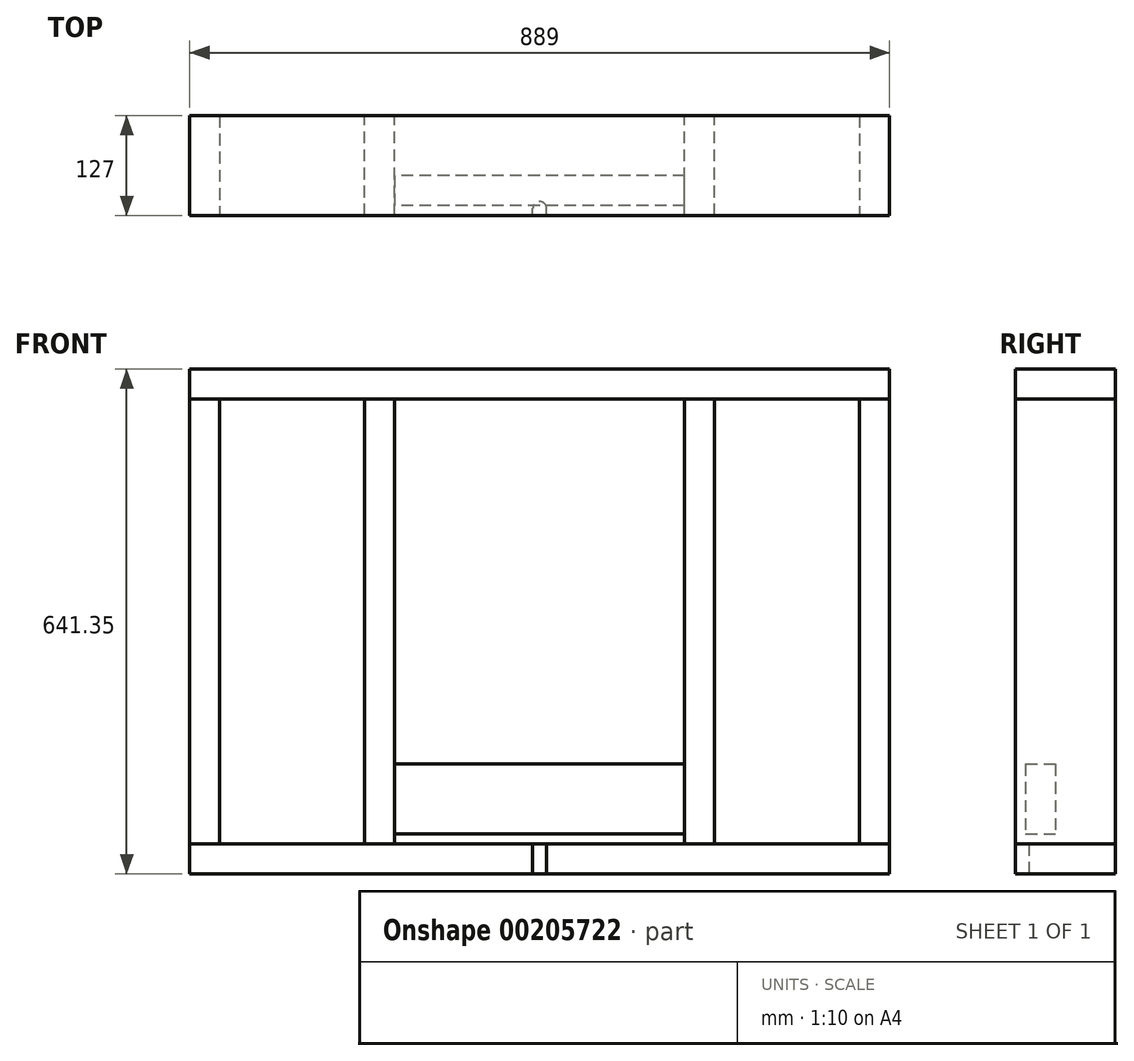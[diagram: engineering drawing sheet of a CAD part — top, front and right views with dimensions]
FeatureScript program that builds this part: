
annotation { "Feature Type Name" : "Feature", "Feature Type Description" : "" }
export const myFeature = defineFeature(function(context is Context, id is Id, definition is map)
    precondition{}
    {
        {
            var Q0;
            Q0=qCreatedBy(makeId("Top.planeOp"),FACE);
            var sketch = newSketch(context, id + "F0", { "sketchPlane" : qUnion([Q0])});
            skLineSegment(sketch, "E0.bottom", {"start": v(444.5, -63.5) * mm, "end": v(-444.5, -63.5) * mm});
            skLineSegment(sketch, "E0.top", {"start": v(444.5, 63.5) * mm, "end": v(-444.5, 63.5) * mm});
            skLineSegment(sketch, "E0.left", {"start": v(444.5, -63.5) * mm, "end": v(444.5, 63.5) * mm});
            skLineSegment(sketch, "E0.right", {"start": v(-444.5, -63.5) * mm, "end": v(-444.5, 63.5) * mm});
            skPoint(sketch, "E0.middle", {"position": v(0, 0) * mm});
            skSolve(sketch);
        }
        {
            var Q0;
            Q0 = qSketchRegion(id + "F0", true);
            extrude(context, id + "F1", {"entities" : qUnion([Q0]), "depth" : 38.1 * mm});
        }
        {
            var Q0;
            Q0=makeQuery(id+"F1.opExtrude","CAP_FACE",FACE,{"disambiguationData":[OSD([sQuery(id+"F0.wireOp",EDGE,"E0.bottom"),sQuery(id+"F0.wireOp",EDGE,"E0.top"),sQuery(id+"F0.wireOp",EDGE,"E0.left"),sQuery(id+"F0.wireOp",EDGE,"E0.right")])],"isStart":false});
            var sketch = newSketch(context, id + "F2", { "sketchPlane" : qUnion([Q0])});
            skLineSegment(sketch, "E1.bottom", {"start": v(-444.5, 63.5) * mm, "end": v(-406.4, 63.5) * mm});
            skLineSegment(sketch, "E1.top", {"start": v(-444.5, -63.5) * mm, "end": v(-406.4, -63.5) * mm});
            skLineSegment(sketch, "E1.left", {"start": v(-444.5, 63.5) * mm, "end": v(-444.5, -63.5) * mm});
            skLineSegment(sketch, "E1.right", {"start": v(-406.4, 63.5) * mm, "end": v(-406.4, -63.5) * mm});
            skSolve(sketch);
        }
        {
            var Q0;
            Q0 = qSketchRegion(id + "F2", true);
            extrude(context, id + "F3", {"entities" : qUnion([Q0]), "depth" : 565.15 * mm});
        }
        {
            var Q0;
            Q0=makeQuery(id+"F3.opExtrude","SWEPT_BODY",BODY,{"disambiguationData":[OSD([sQuery(id+"F2.wireOp",EDGE,"E1.bottom"),sQuery(id+"F2.wireOp",EDGE,"E1.top"),sQuery(id+"F2.wireOp",EDGE,"E1.left"),sQuery(id+"F2.wireOp",EDGE,"E1.right")])]});
            var Q1;
            Q1=qCreatedBy(makeId("Right.planeOp"),FACE);
            mirror(context, id + "F4", {"entities" : qUnion([Q0]), "mirrorPlane" : qUnion([Q1])});
        }
        {
            var Q0;
            Q0=makeQuery(id+"F3.opExtrude","CAP_FACE",FACE,{"disambiguationData":[OSD([sQuery(id+"F2.wireOp",EDGE,"E1.bottom"),sQuery(id+"F2.wireOp",EDGE,"E1.top"),sQuery(id+"F2.wireOp",EDGE,"E1.left"),sQuery(id+"F2.wireOp",EDGE,"E1.right")])],"isStart":false});
            var sketch = newSketch(context, id + "F5", { "sketchPlane" : qUnion([Q0])});
            skLineSegment(sketch, "E2.bottom", {"start": v(-444.5, 63.5) * mm, "end": v(444.5, 63.5) * mm});
            skLineSegment(sketch, "E2.top", {"start": v(-444.5, -63.5) * mm, "end": v(444.5, -63.5) * mm});
            skLineSegment(sketch, "E2.left", {"start": v(-444.5, 63.5) * mm, "end": v(-444.5, -63.5) * mm});
            skLineSegment(sketch, "E2.right", {"start": v(444.5, 63.5) * mm, "end": v(444.5, -63.5) * mm});
            skSolve(sketch);
        }
        {
            var Q0;
            {var subQ2=sQuery(id+"F5.wireOp",EDGE,"E2.right");Q0=makeQuery(id+"F5.imprint","IMPRINT",FACE,{"disambiguationData":[TD([[makeQuery(id+"F5.imprint","IMPRINT",EDGE,{"derivedFrom":subQ2}),-1.0]])]});}
            var Q1;
            {var subQ0=sQuery(id+"F5.wireOp",EDGE,"E2.left");Q1=makeQuery(id+"F5.imprint","IMPRINT",FACE,{"disambiguationData":[TD([[makeQuery(id+"F5.imprint","IMPRINT",EDGE,{"derivedFrom":subQ0}),-1.0]])]});}
            extrude(context, id + "F6", {"entities" : qUnion([Q0, Q1]), "depth" : 38.1 * mm});
        }
        {
            var Q0;
            Q0=makeQuery(id+"F1.opExtrude","CAP_FACE",FACE,{"disambiguationData":[OSD([sQuery(id+"F0.wireOp",EDGE,"E0.bottom"),sQuery(id+"F0.wireOp",EDGE,"E0.top"),sQuery(id+"F0.wireOp",EDGE,"E0.left"),sQuery(id+"F0.wireOp",EDGE,"E0.right")])],"isStart":false});
            var sketch = newSketch(context, id + "F7", { "sketchPlane" : qUnion([Q0])});
            skPoint(sketch, "E3", {"position": v(-203.2, 0) * mm});
            skLineSegment(sketch, "E4.bottom", {"start": v(-184.15, -63.5) * mm, "end": v(-222.25, -63.5) * mm});
            skLineSegment(sketch, "E4.top", {"start": v(-184.15, 63.5) * mm, "end": v(-222.25, 63.5) * mm});
            skLineSegment(sketch, "E4.left", {"start": v(-184.15, -63.5) * mm, "end": v(-184.15, 63.5) * mm});
            skLineSegment(sketch, "E4.right", {"start": v(-222.25, -63.5) * mm, "end": v(-222.25, 63.5) * mm});
            skLineSegment(sketch, "E5.MirrorCS", {"start": v(184.15, -63.5) * mm, "end": v(184.15, 63.5) * mm});
            skLineSegment(sketch, "E6.MirrorCS", {"start": v(222.25, -63.5) * mm, "end": v(222.25, 63.5) * mm});
            skLineSegment(sketch, "E7.MirrorCS", {"start": v(184.15, 63.5) * mm, "end": v(222.25, 63.5) * mm});
            skLineSegment(sketch, "E8.MirrorCS", {"start": v(184.15, -63.5) * mm, "end": v(222.25, -63.5) * mm});
            skSolve(sketch);
        }
        {
            var Q0;
            Q0 = qSketchRegion(id + "F7", true);
            extrude(context, id + "F8", {"entities" : qUnion([Q0]), "endBound" : BoundingType.UP_TO_NEXT, "depth" : 25.4 * mm});
        }
        {
            var Q0;
            Q0=makeQuery(id+"F8.opExtrude","SWEPT_FACE",FACE,{"disambiguationData":[OSD([sQuery(id+"F7.wireOp",EDGE,"E4.left")])]});
            var sketch = newSketch(context, id + "F9", { "sketchPlane" : qUnion([Q0])});
            skLineSegment(sketch, "E9.bottom", {"start": v(-12.7, 50.8) * mm, "end": v(-50.8, 50.8) * mm});
            skLineSegment(sketch, "E9.top", {"start": v(-12.7, 139.7) * mm, "end": v(-50.8, 139.7) * mm});
            skLineSegment(sketch, "E9.left", {"start": v(-12.7, 50.8) * mm, "end": v(-12.7, 139.7) * mm});
            skLineSegment(sketch, "E9.right", {"start": v(-50.8, 50.8) * mm, "end": v(-50.8, 139.7) * mm});
            skPoint(sketch, "E9.middle", {"position": v(-31.75, 95.25) * mm});
            skSolve(sketch);
        }
        {
            var Q0;
            Q0 = qSketchRegion(id + "F9", true);
            extrude(context, id + "F10", {"entities" : qUnion([Q0]), "endBound" : BoundingType.UP_TO_NEXT, "depth" : 25.4 * mm});
        }
        {
            var Q0;
            Q0=makeQuery(id+"F1.opExtrude","CAP_FACE",FACE,{"disambiguationData":[OSD([sQuery(id+"F0.wireOp",EDGE,"E0.bottom"),sQuery(id+"F0.wireOp",EDGE,"E0.top"),sQuery(id+"F0.wireOp",EDGE,"E0.left"),sQuery(id+"F0.wireOp",EDGE,"E0.right")])],"isStart":false});
            var sketch = newSketch(context, id + "F11", { "sketchPlane" : qUnion([Q0])});
            skArc(sketch, "E10", {"start": v(8.9, -54.6) * mm, "mid": v(0, -45.72) * mm, "end": v(-8.9, -54.6) * mm});
            skLineSegment(sketch, "E11", {"start": v(-8.9, -54.6) * mm, "end": v(-8.9, -63.5) * mm});
            skLineSegment(sketch, "E12", {"start": v(8.89, -54.6) * mm, "end": v(8.9, -63.5) * mm});
            skSolve(sketch);
        }
        {
            var Q0;
            Q0 = qSketchRegion(id + "F11", true);
            var Q1;
            Q1=makeQuery(id+"F11.imprint","IMPRINT",FACE,{"disambiguationData":[TD([[makeQuery(id+"F11.imprint","IMPRINT",EDGE,{"derivedFrom":sQuery(id+"F11.wireOp",EDGE,"E10")}),1.0]])]});
            extrude(context, id + "F12", {"entities" : qUnion([Q0, Q1]), "operationType" : NewBodyOperationType.REMOVE, "endBound" : BoundingType.UP_TO_NEXT, "oppositeDirection" : true, "depth" : 25.4 * mm});
        }
    });
